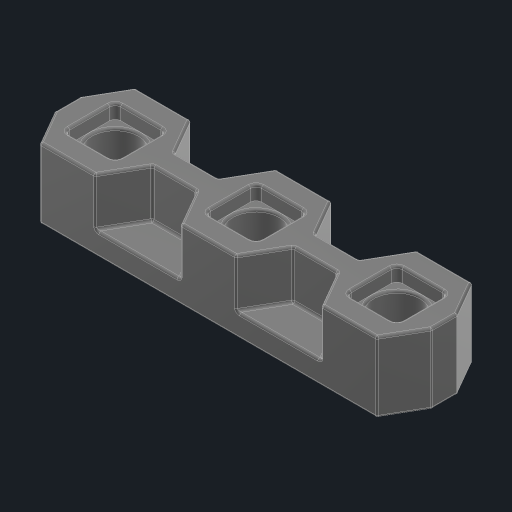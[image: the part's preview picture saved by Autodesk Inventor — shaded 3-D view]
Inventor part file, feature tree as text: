
AUTODESK INVENTOR PART (.ipt)
format: ipt  version: 2023 (Build 270158030, 158C)  size: 359,936 bytes
history: native  units: in
note: dims shown in document units (in); Inventor stores cm internally (conversion verified against a paired STEP export)
features: fillet x1, extrude x1, sketch x1
ambient origin geometry x8: Origin, YZ Plane, XZ Plane, XY Plane, X Axis, Y Axis, Z Axis, Center Point
bodies: Solid1 (feature_tree)
feature tree (3):
  fillet  "Fillet6"  Radius=0.0394in
  extrude  "Extrusion1"  [1 undecoded]
  sketch  "Sketch1"
note: 1 required parameter value undecoded (feature->parameter linkage not recoverable at this tier; creation-order binding heuristic only, values carry confidence <= 0.55)
